# Revit family: LPKB Silent 125 C1 EC_7540624
name_source: partatom
category: Mechanical Equipment
revit_build: Autodesk Revit MEP 2014 (Build: 20130308_1515(x64)
units: mm (PartAtom-declared; Revit-internal decimal feet)

## types (1)
- LPKB Silent 125 C1 EC
    Capacitor = -
    Current = 1 A
    Depth = 330 mm  [stored 1.08268 ft]
    Description = SOUND ATTENUATED DUCT FANS WITH CIRCULAR CONNECTIONS
    Diameter = 125 mm  [stored 0.410105 ft]
    Distance 1 = 73 mm  [stored 0.239501 ft]
    Distance 2 = 190 mm
    Frequency = 50 Hz
    Height = 210 mm  [stored 0.688976 ft]
    Main Material = Steel, Galvanized
    Max. temperature of transported air = 60 °C
    Max. temperature of transported air when speed controlled = 60 °C
    Phase = 1
    Power = 116 W
    Radius = 63 mm
    Sound pressure level at 3 m = 55
    Speed = 3670
    Vertical Distance = 124 mm
    Voltage = 230 V
    Voltage range = 200-240
    Weight = 6.20 kg
    Width = 410 mm  [stored 1.34514 ft]
    Width A = 314 mm
    Wiring diagram = 4040143

note: [stored X ft] marks values corroborated as IEEE doubles in the binary element streams (Revit-internal decimal feet)

## geometry (parser evidence)
native form markers: Sweep x6
no freeform markers — native parametric forms only
